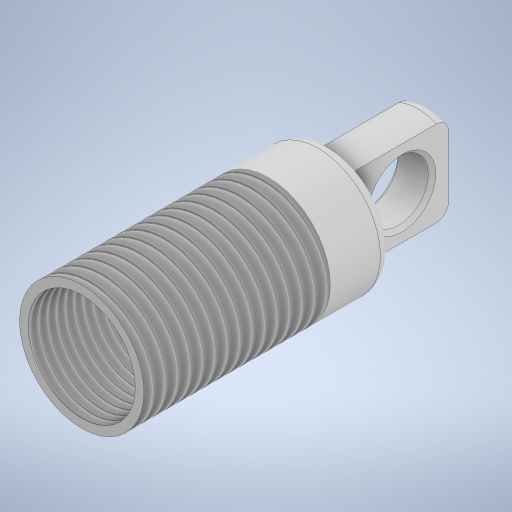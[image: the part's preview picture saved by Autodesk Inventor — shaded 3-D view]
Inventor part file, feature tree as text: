
AUTODESK INVENTOR PART (.ipt)
format: ipt  version: 2024 (Build 280153000, 153)  size: 342,528 bytes
history: native  units: in
note: dims shown in document units (in); Inventor stores cm internally (conversion verified against a paired STEP export)
features: extrude x4, sketch x4, fillet x2, thread x2, shell x1, chamfer x1, projected_geometry x1
ambient origin geometry x8: Origin, YZ Plane, XZ Plane, XY Plane, X Axis, Y Axis, Z Axis, Center Point
bodies: Solid1 (feature_tree)
feature tree (15):
  extrude  "Extrusion1"  Depth=0.05in TaperAngle=0.0deg
  shell  "Shell1"  Thickness=0.035in
  fillet  "Fillet1"  Radius=0.05in
  extrude  "Extrusion2"  Depth=0.4in TaperAngle=0.0deg
  extrude  "Extrusion3"  Depth=0.4in TaperAngle=0.0deg
  extrude  "Extrusion4"  Depth=0.05in
  chamfer  "Chamfer1"  [1 undecoded]
  fillet  "Fillet2"  Radius=0.015in
  thread  "Thread1"  [1 undecoded]
  thread  "Thread2"  [1 undecoded]
  sketch  "Sketch1"  dims[d0=0.5in d1=1.0in d2=0.0in d3=0.035in d4=0.05in]
  sketch  "Sketch2"  dims[d5=0.375in d6=0.4in d7=0.0in]
  sketch  "Sketch3"  dims[d8=0.15in d9=0.4in d10=0.0in]
  sketch  "Sketch4"  dims[d11=0.24in d12=0.1875in d13=0.0in d14=0.0in d15=0.015in d16=0.125in d17=45.0deg d18=0.05in d19=1.0236in d20=0.2in d21=1.0236in d22=0.575in]
  projected_geometry  "Project Cut Edges1"
note: 3 required parameter values undecoded (feature->parameter linkage not recoverable at this tier; creation-order binding heuristic only, values carry confidence <= 0.55)
